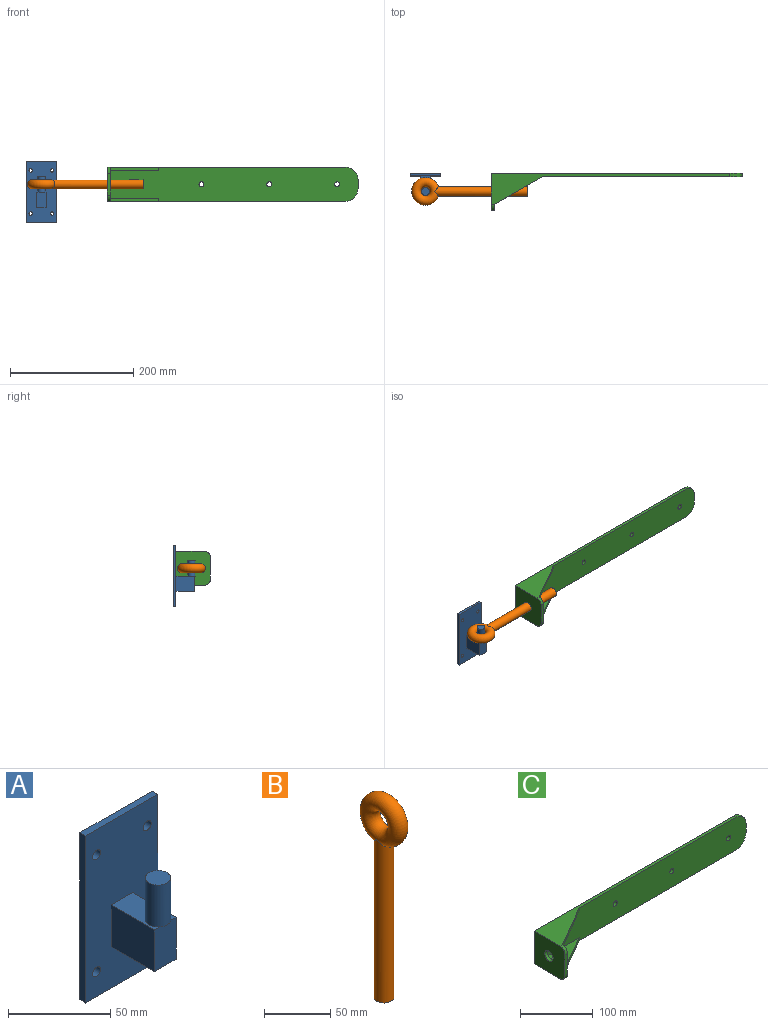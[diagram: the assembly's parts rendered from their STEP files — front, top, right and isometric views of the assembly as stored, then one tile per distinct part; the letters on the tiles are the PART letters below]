
ASSEMBLY  parts=3 mates=2
PART A: 18 faces, bbox 50x35.3x100 mm
  f0: plane 100x50mm, normal (0,-1,0), area 4530mm2, adj f1,f2,f3,f4,f5,f6,f7,f8
  f1: plane 50x4mm, normal (0,0,-1), area 200mm2, adj f0,f2,f8,f9
  f2: plane 100x4mm, normal (1,0,0), area 400mm2, adj f0,f1,f3,f9
  f3: plane 50x4mm, normal (0,0,1), area 200mm2, adj f0,f2,f8,f9
  f4: cylinder r=2.75mm len=5.5mm, axis (0,1,0), area 69.1mm2, adj f0,f9
  f5: cylinder r=2.75mm len=5.5mm, axis (0,1,0), area 69.1mm2, adj f0,f9
  f6: cylinder r=2.75mm len=5.5mm, axis (0,1,0), area 69.1mm2, adj f0,f9
  f7: cylinder r=2.75mm len=5.5mm, axis (0,1,0), area 69.1mm2, adj f0,f9
  f8: plane 100x4mm, normal (-1,0,0), area 400mm2, adj f0,f1,f3,f9
  f9: plane 100x50mm, normal (0,1,0), area 4905mm2, adj f1,f2,f3,f4,f5,f6,f7,f8
  f10: plane 30x15mm, normal (0,0,-1), area 450mm2, adj f0,f11,f13,f14
  f11: plane 30x25mm, normal (1,0,0), area 750mm2, adj f0,f10,f12,f14
  f12: plane 30x15mm, normal (0,0,1), area 333.7mm2, adj f0,f11,f13,f14,f15
  f13: plane 30x25mm, normal (-1,0,0), area 750mm2, adj f0,f10,f12,f14
  f14: plane 25x15mm, normal (0,-1,0), area 375mm2, adj f10,f11,f12,f13,f17
  f15: cylinder r=6.25mm len=25mm, axis (0,0,-1), area 981.7mm2, adj f12,f16,f17
  f16: plane 12.5x12.5mm, normal (0,0,1), area 122.7mm2, adj f15
  f17: plane 7.5x1.25mm, normal (0,0,-1), area 6.4mm2, adj f14,f15
PART B: 3 faces, bbox 15x48.7x189.4 mm
  f0: torus R=15mm, axis (1,0,0), area 4213.1mm2, adj f1
  f1: cylinder r=7.5mm len=150mm, axis (0,0,1), area 6875.4mm2, adj f0,f2
  f2: plane 15x15mm, normal (0,0,-1), area 176.7mm2, adj f1
PART C: 24 faces, bbox 406.4x60x55 mm
  f0: plane 406.4x55mm, normal (0,1,0), area 21804.5mm2, adj f3,f4,f5,f6,f7,f8,f17,f18
  f1: plane 401.4x55mm, normal (0,-1,0), area 20750.1mm2, adj f2,f3,f4,f5,f6,f7,f10,f11
  f2: plane 77.94x45mm, normal (0.5,-0.87,0), area 450mm2, adj f1,f4,f10,f12
  f3: plane 15x5mm, normal (1,0,0), area 75mm2, adj f0,f1,f5,f6
  f4: plane 386.4x50mm, normal (0,0,-1), area 3910.7mm2, adj f0,f1,f2,f5,f8,f15
  f5: cylinder r=20mm len=20mm, axis (0,1,0), area 157.1mm2, adj f0,f1,f3,f4
  f6: cylinder r=20mm len=20mm, axis (0,1,0), area 157.1mm2, adj f0,f1,f3,f7
  f7: plane 386.4x50mm, normal (0,0,1), area 3910.7mm2, adj f0,f1,f6,f8,f11,f14
  f8: plane 60x55mm, normal (-1,0,0), area 3056mm2, adj f0,f4,f7,f9,f14,f15,f16
  f9: plane 35x5mm, normal (0,-1,0), area 175mm2, adj f8,f10,f14,f15
  f10: plane 55x55mm, normal (1,0,0), area 2331mm2, adj f1,f2,f9,f11,f12,f13,f14,f15
  f11: plane 77.94x45mm, normal (0.5,-0.87,0), area 450mm2, adj f1,f7,f10,f13
  f12: plane 77.94x45mm, normal (0,0,1), area 1753.7mm2, adj f1,f2,f10
  f13: plane 77.94x45mm, normal (0,0,-1), area 1753.7mm2, adj f1,f10,f11
  f14: cylinder r=10mm len=10mm, axis (1,0,0), area 78.5mm2, adj f7,f8,f9,f10
  f15: cylinder r=10mm len=10mm, axis (-1,0,0), area 78.5mm2, adj f4,f8,f9,f10
  f16: cylinder r=8mm len=16mm, axis (1,0,0), area 251.3mm2, adj f8,f10
  f17: plane 15x5mm, normal (0,0,1), area 75mm2, adj f0,f1,f18,f20
  f18: plane 15x5mm, normal (-1,0,0), area 75mm2, adj f0,f1,f17,f19
  f19: plane 15x5mm, normal (0,0,-1), area 75mm2, adj f0,f1,f18,f20
  f20: plane 15x5mm, normal (1,0,0), area 75mm2, adj f0,f1,f17,f19
  f21: cylinder r=4mm len=8mm, axis (0,-1,0), area 125.7mm2, adj f0,f1
  f22: cylinder r=4mm len=8mm, axis (0,-1,0), area 125.7mm2, adj f0,f1
  f23: cylinder r=4mm len=8mm, axis (0,-1,0), area 125.7mm2, adj f0,f1
PLACE A t=(-1593.15,-195.04,-192.21)mm
PLACE B rot(axis=(0.71,0,-0.71),180deg) t=(-1428.15,-324.04,-179.71)mm
PLACE C t=(-1626.53,-195.04,-179.71)mm
MATE revolute A.f15 <-> B.f0  axis (0,0,-1) through (-1593.15,-224.04,-179.71)mm
MATE revolute B.f1 <-> C.f16  axis (-1,0,0) through (-1503.6,-224.04,-179.71)mm
